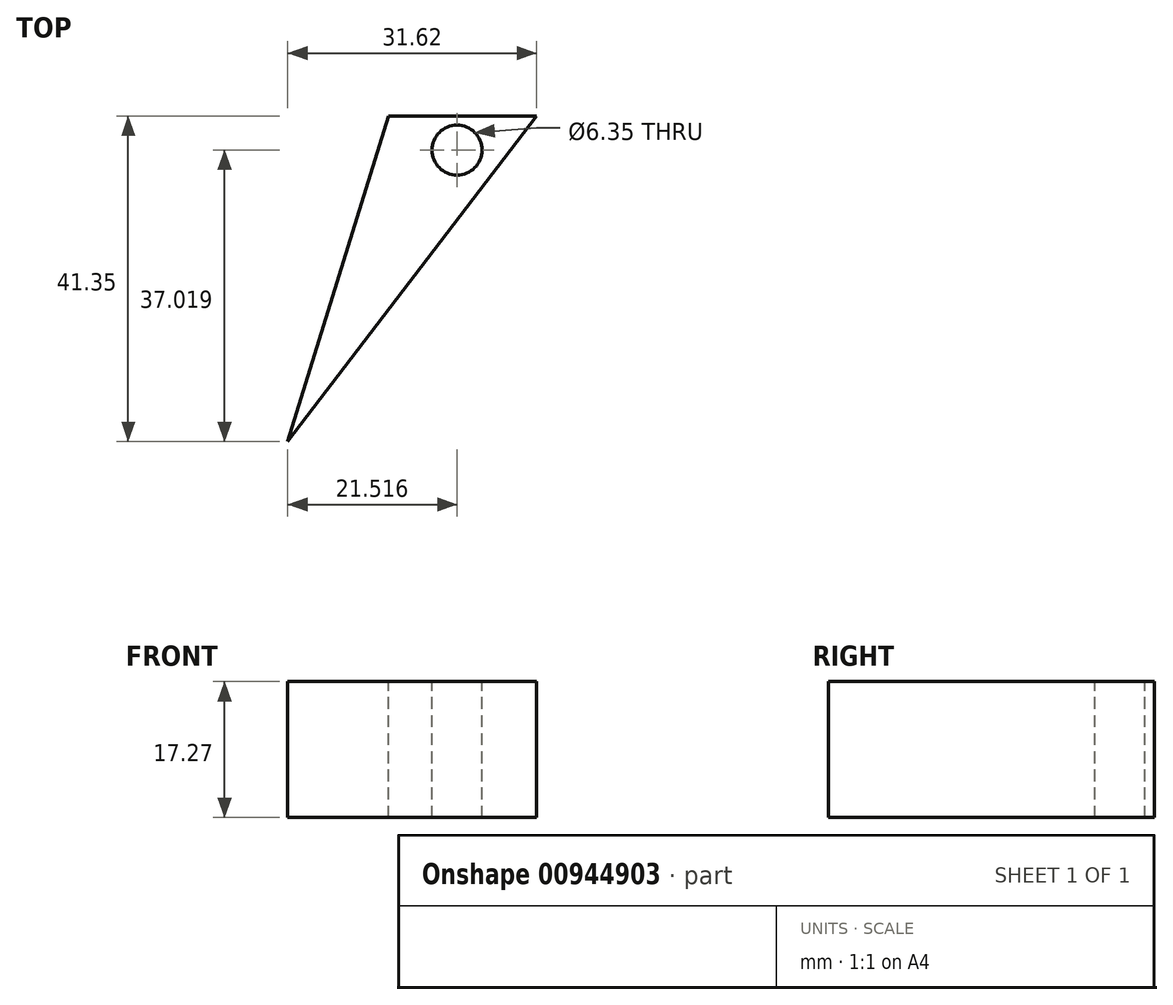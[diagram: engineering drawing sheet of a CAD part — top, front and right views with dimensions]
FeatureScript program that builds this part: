
annotation { "Feature Type Name" : "Feature", "Feature Type Description" : "" }
export const myFeature = defineFeature(function(context is Context, id is Id, definition is map)
    precondition{}
    {
        {
            var Q0;
            Q0=qCreatedBy(makeId("Top.planeOp"),FACE);
            var sketch = newSketch(context, id + "F0", { "sketchPlane" : qUnion([Q0])});
            skLineSegment(sketch, "E0", {"start": v(-128.8, 26.62) * mm, "end": v(-134.25, -41.35) * mm});
            skLineSegment(sketch, "E1", {"start": v(-134.25, -41.35) * mm, "end": v(-102.63, 0) * mm});
            skLineSegment(sketch, "E2", {"start": v(-102.63, 0) * mm, "end": v(-128.8, 26.62) * mm});
            skPoint(sketch, "E3", {"position": v(-121.43, 0) * mm});
            skLineSegment(sketch, "E4", {"start": v(-134.25, -41.35) * mm, "end": v(-121.43, 0) * mm});
            skLineSegment(sketch, "E5", {"start": v(-121.43, 0) * mm, "end": v(-128.8, 26.62) * mm});
            skLineSegment(sketch, "E6", {"start": v(-102.63, 0) * mm, "end": v(-121.43, 0) * mm});
            skSolve(sketch);
        }
        {
            var Q0;
            Q0=makeQuery(id+"F0.imprint","IMPRINT",FACE,{"disambiguationData":[TD([[makeQuery(id+"F0.imprint","IMPRINT",EDGE,{"derivedFrom":sQuery(id+"F0.wireOp",EDGE,"E1")}),1.0]])]});
            extrude(context, id + "F1", {"entities" : qUnion([Q0]), "oppositeDirection" : true, "depth" : 17.27 * mm, "offsetDistance" : 25.4 * mm});
        }
        {
            var Q0;
            Q0=makeQuery(id+"F1.opExtrude","CAP_FACE",FACE,{"disambiguationData":[OSD([sQuery(id+"F0.wireOp",EDGE,"E1"),sQuery(id+"F0.wireOp",EDGE,"E4"),sQuery(id+"F0.wireOp",EDGE,"E6")])],"isStart":true});
            var sketch = newSketch(context, id + "F2", { "sketchPlane" : qUnion([Q0])});
            skCircle(sketch, "E7", {"center": v(-112.73, -4.33) * mm, "radius": 3.61 * mm});
            skSolve(sketch);
        }
        {
            var Q0;
            Q0=sQuery(id+"F2.wireOp",VERTEX,"E7.center");
            var Q1;
            Q1=makeQuery(id+"F1.opExtrude","SWEPT_BODY",BODY,{"disambiguationData":[OSD([sQuery(id+"F0.wireOp",EDGE,"E1"),sQuery(id+"F0.wireOp",EDGE,"E4"),sQuery(id+"F0.wireOp",EDGE,"E6")])]});
            hole(context, id + "F3", {"style" : HoleStyle.SIMPLE, "endStyle" : HoleEndStyle.THROUGH, "holeDiameter" : 6.35 * mm, "majorDiameter" : 6.35 * mm, "isTappedThrough" : true, "tappedDepth" : 12.7 * mm, "tapClearance" : 3, "locations" : qUnion([Q0]), "scope" : qUnion([Q1])});
        }
    });
